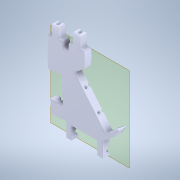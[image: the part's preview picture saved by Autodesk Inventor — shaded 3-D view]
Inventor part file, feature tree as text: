
AUTODESK INVENTOR PART (.ipt)
format: ipt  version: 2022 (Build 260153000, 153)  size: 736,768 bytes
history: native  units: mm
features: other x6, sketch x4, fillet x3, extrude x3, plane x1
ambient origin geometry x8: Origin, YZ Plane, XZ Plane, XY Plane, X Axis, Y Axis, Z Axis, Center Point
bodies: Body1 (feature_tree)
feature tree (17):
  other  "Sólido1"
  other  "Edición directa1"
  fillet  "Empalme9"  Radius=2.0mm
  fillet  "Empalme10"  Radius=2.0mm
  fillet  "Empalme11"  Radius=2.0mm
  extrude  "Extrusión4"  Depth=10.0mm TaperAngle=0.0deg
  extrude  "Extrusión5"  TaperAngle=0.0deg  [1 undecoded]
  other  "Edición directa2"
  sketch  "Boceto6"  dims[d25=10.0mm d26=0.0mm d27=0.0mm d28=0.0mm d29=-1.0mm]
  extrude  "Extrusión6"  Depth=10.0mm TaperAngle=0.0deg
  plane  "Plano de trabajo1"
  sketch  "Boceto4"  dims[d10=0.0mm d11=0.0mm d12=4.0mm d13=2.0mm d19=2.0mm d20=2.0mm]
  sketch  "Boceto5"  dims[d22=60.0mm d23=10.0mm d24=0.0mm]
  sketch  "Boceto7"  dims[d30=3.88mm d31=10.0mm d32=0.0mm d38=-8.5mm d5=0.0mm d6=0.0mm d7=0.0mm d8=0.0mm]
  other  "LPattern5"
  other  "Desplazar1"
  other  "Desplazar2"
note: 1 required parameter value undecoded (feature->parameter linkage not recoverable at this tier; creation-order binding heuristic only, values carry confidence <= 0.55)
